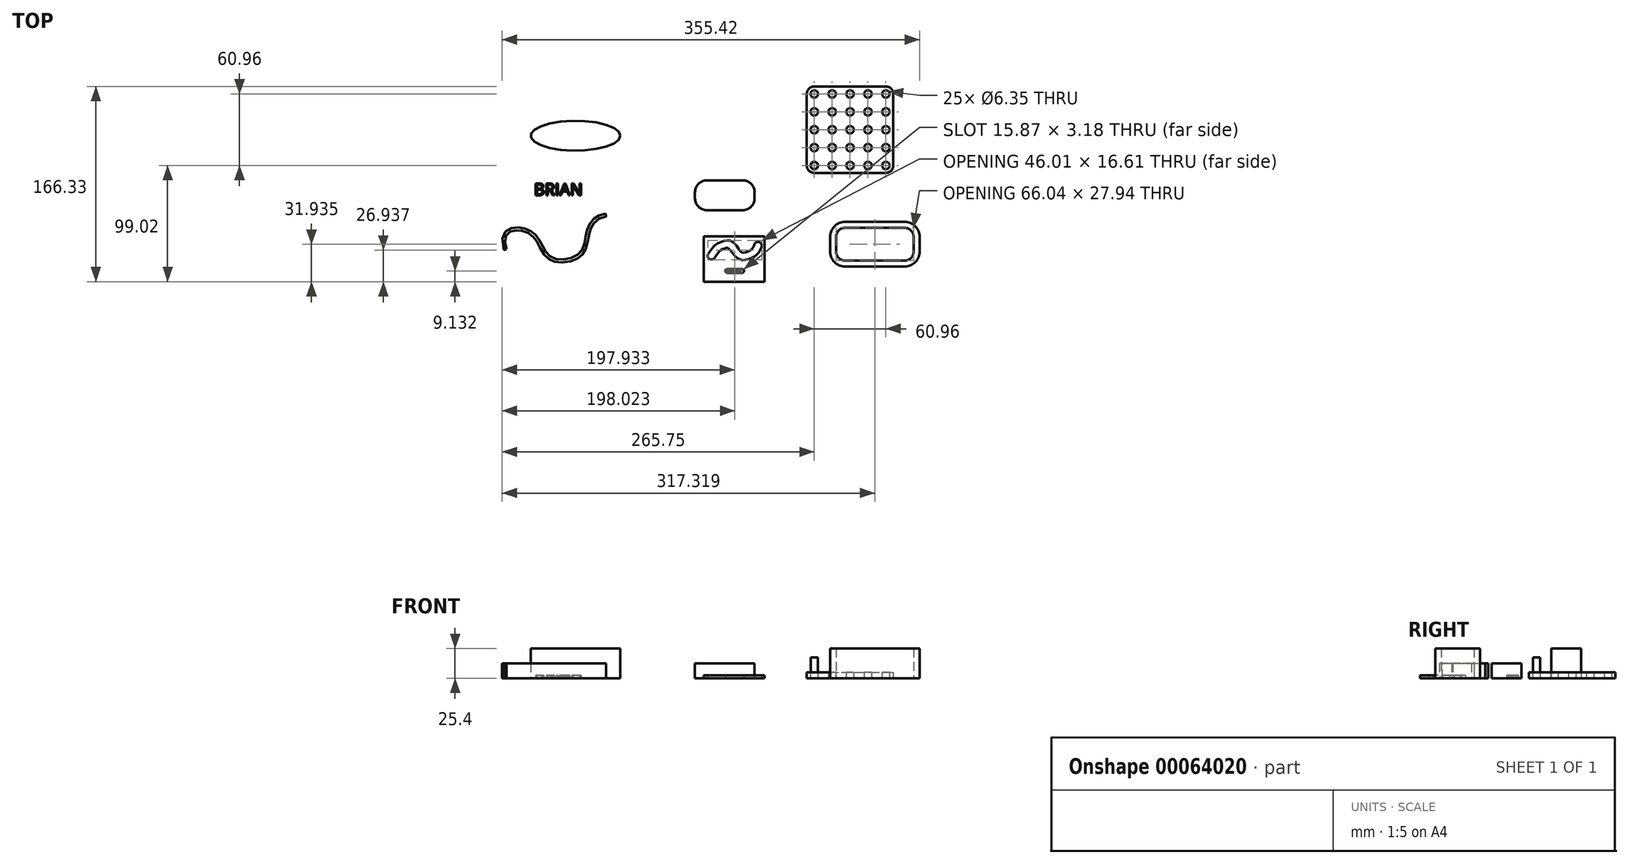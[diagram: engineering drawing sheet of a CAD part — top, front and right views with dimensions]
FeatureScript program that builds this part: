
annotation { "Feature Type Name" : "Feature", "Feature Type Description" : "" }
export const myFeature = defineFeature(function(context is Context, id is Id, definition is map)
    precondition{}
    {
        {
            var Q0;
            Q0=qCreatedBy(makeId("Top.planeOp"),FACE);
            var sketch = newSketch(context, id + "F0", { "sketchPlane" : qUnion([Q0])});
            skLineSegment(sketch, "E0.rect.bottom", {"start": v(15.24, 12.7) * mm, "end": v(-15.24, 12.7) * mm});
            skLineSegment(sketch, "E0.rect.top", {"start": v(15.24, -12.7) * mm, "end": v(-15.24, -12.7) * mm});
            skLineSegment(sketch, "E0.rect.left", {"start": v(25.4, 2.54) * mm, "end": v(25.4, -2.54) * mm});
            skLineSegment(sketch, "E0.rect.right", {"start": v(-25.4, 2.54) * mm, "end": v(-25.4, -2.54) * mm});
            skPoint(sketch, "E0.rect.middle", {"position": v(0, 0) * mm});
            skPoint(sketch, "E1.visualSharp", {"position": v(25.4, 12.7) * mm});
            skArc(sketch, "E1.filletArc", {"start": v(25.4, 2.54) * mm, "mid": v(22.42, 9.72) * mm, "end": v(15.24, 12.7) * mm});
            skPoint(sketch, "E2.visualSharp", {"position": v(25.4, -12.7) * mm});
            skArc(sketch, "E2.filletArc", {"start": v(15.24, -12.7) * mm, "mid": v(22.42, -9.72) * mm, "end": v(25.4, -2.54) * mm});
            skPoint(sketch, "E3.visualSharp", {"position": v(-25.4, 12.7) * mm});
            skArc(sketch, "E3.filletArc", {"start": v(-15.24, 12.7) * mm, "mid": v(-22.42, 9.72) * mm, "end": v(-25.4, 2.54) * mm});
            skPoint(sketch, "E4.visualSharp", {"position": v(-25.4, -12.7) * mm});
            skArc(sketch, "E4.filletArc", {"start": v(-25.4, -2.54) * mm, "mid": v(-22.42, -9.72) * mm, "end": v(-15.24, -12.7) * mm});
            skSolve(sketch);
        }
        {
            var Q0;
            Q0 = qSketchRegion(id + "F0", true);
            extrude(context, id + "F1", {"entities" : qUnion([Q0]), "depth" : 12.7 * mm});
        }
        {
            var Q0;
            Q0=qCreatedBy(makeId("Top.planeOp"),FACE);
            var sketch = newSketch(context, id + "F2", { "sketchPlane" : qUnion([Q0])});
            skCircle(sketch, "E5", {"center": v(76.2, 25.4) * mm, "radius": 3.18 * mm});
            skCircle(sketch, "E6.0.1.0", {"center": v(76.2, 40.64) * mm, "radius": 3.18 * mm});
            skCircle(sketch, "E6.0.2.0", {"center": v(76.2, 55.88) * mm, "radius": 3.18 * mm});
            skCircle(sketch, "E6.0.3.0", {"center": v(76.2, 71.12) * mm, "radius": 3.18 * mm});
            skCircle(sketch, "E6.0.4.0", {"center": v(76.2, 86.36) * mm, "radius": 3.18 * mm});
            skCircle(sketch, "E6.1.0.0", {"center": v(91.44, 25.4) * mm, "radius": 3.18 * mm});
            skCircle(sketch, "E6.1.1.0", {"center": v(91.44, 40.64) * mm, "radius": 3.18 * mm});
            skCircle(sketch, "E6.1.2.0", {"center": v(91.44, 55.88) * mm, "radius": 3.18 * mm});
            skCircle(sketch, "E6.1.3.0", {"center": v(91.44, 71.12) * mm, "radius": 3.18 * mm});
            skCircle(sketch, "E6.1.4.0", {"center": v(91.44, 86.36) * mm, "radius": 3.18 * mm});
            skCircle(sketch, "E6.2.0.0", {"center": v(106.68, 25.4) * mm, "radius": 3.18 * mm});
            skCircle(sketch, "E6.2.1.0", {"center": v(106.68, 40.64) * mm, "radius": 3.18 * mm});
            skCircle(sketch, "E6.2.2.0", {"center": v(106.68, 55.88) * mm, "radius": 3.18 * mm});
            skCircle(sketch, "E6.2.3.0", {"center": v(106.68, 71.12) * mm, "radius": 3.18 * mm});
            skCircle(sketch, "E6.2.4.0", {"center": v(106.68, 86.36) * mm, "radius": 3.18 * mm});
            skCircle(sketch, "E6.3.0.0", {"center": v(121.92, 25.4) * mm, "radius": 3.18 * mm});
            skCircle(sketch, "E6.3.1.0", {"center": v(121.92, 40.64) * mm, "radius": 3.18 * mm});
            skCircle(sketch, "E6.3.2.0", {"center": v(121.92, 55.88) * mm, "radius": 3.18 * mm});
            skCircle(sketch, "E6.3.3.0", {"center": v(121.92, 71.12) * mm, "radius": 3.18 * mm});
            skCircle(sketch, "E6.3.4.0", {"center": v(121.92, 86.36) * mm, "radius": 3.18 * mm});
            skCircle(sketch, "E6.4.0.0", {"center": v(137.16, 25.4) * mm, "radius": 3.18 * mm});
            skCircle(sketch, "E6.4.1.0", {"center": v(137.16, 40.64) * mm, "radius": 3.18 * mm});
            skCircle(sketch, "E6.4.2.0", {"center": v(137.16, 55.88) * mm, "radius": 3.18 * mm});
            skCircle(sketch, "E6.4.3.0", {"center": v(137.16, 71.12) * mm, "radius": 3.18 * mm});
            skCircle(sketch, "E6.4.4.0", {"center": v(137.16, 86.36) * mm, "radius": 3.18 * mm});
            skLineSegment(sketch, "E6.direction1", {"start": v(76.2, 25.4) * mm, "end": v(91.44, 25.4) * mm, "construction": true});
            skLineSegment(sketch, "E6.direction2", {"start": v(76.2, 25.4) * mm, "end": v(76.2, 40.64) * mm, "construction": true});
            skLineSegment(sketch, "E7.bottom", {"start": v(76.2, 92.7) * mm, "end": v(137.16, 92.7) * mm});
            skLineSegment(sketch, "E7.top", {"start": v(76.2, 19.05) * mm, "end": v(137.16, 19.05) * mm});
            skLineSegment(sketch, "E7.left", {"start": v(69.85, 86.36) * mm, "end": v(69.85, 25.4) * mm});
            skLineSegment(sketch, "E7.right", {"start": v(143.5, 86.36) * mm, "end": v(143.5, 25.4) * mm});
            skPoint(sketch, "E8.visualSharp", {"position": v(143.5, 92.7) * mm});
            skArc(sketch, "E8.filletArc", {"start": v(143.5, 86.36) * mm, "mid": v(141.65, 90.85) * mm, "end": v(137.16, 92.7) * mm});
            skPoint(sketch, "E9.visualSharp", {"position": v(143.5, 19.05) * mm});
            skArc(sketch, "E9.filletArc", {"start": v(137.16, 19.05) * mm, "mid": v(141.65, 20.9) * mm, "end": v(143.5, 25.4) * mm});
            skPoint(sketch, "E10.visualSharp", {"position": v(69.85, 19.05) * mm});
            skArc(sketch, "E10.filletArc", {"start": v(69.85, 25.4) * mm, "mid": v(71.7, 20.9) * mm, "end": v(76.2, 19.05) * mm});
            skPoint(sketch, "E11.visualSharp", {"position": v(69.85, 92.7) * mm});
            skArc(sketch, "E11.filletArc", {"start": v(76.2, 92.7) * mm, "mid": v(71.7, 90.85) * mm, "end": v(69.85, 86.36) * mm});
            skSolve(sketch);
        }
        {
            var Q0;
            Q0 = qSketchRegion(id + "F2", true);
            extrude(context, id + "F3", {"entities" : qUnion([Q0]), "depth" : 5.08 * mm});
        }
        {
            var Q0;
            Q0=qCreatedBy(makeId("Top.planeOp"),FACE);
            var sketch = newSketch(context, id + "F4", { "sketchPlane" : qUnion([Q0])});
            skEllipse(sketch, "E12", {"center": v(-127, 50.8) * mm, "majorRadius": 38.1 * mm, "minorRadius": 12.7 * mm, "majorAxis": v(1, 0)});
            skFitSpline(sketch, "E13.0", {"points": [v(-82.63, 49.22) * mm, v(-82.51, 50.8) * mm, v(-82.63, 52.38) * mm, v(-82.97, 53.89) * mm, v(-83.5, 55.3) * mm, v(-84.4, 57) * mm, v(-85.8, 58.84) * mm, v(-87.78, 60.65) * mm, v(-89.99, 62.2) * mm, v(-92.42, 63.55) * mm, v(-94.65, 64.55) * mm, v(-96.55, 65.29) * mm, v(-98.04, 65.8) * mm, v(-99.59, 66.3) * mm, v(-101.7, 66.9) * mm, v(-104.46, 67.59) * mm, v(-107.92, 68.28) * mm, v(-111.53, 68.84) * mm, v(-115.26, 69.29) * mm, v(-119.1, 69.61) * mm, v(-122.36, 69.77) * mm, v(-125, 69.84) * mm, v(-127, 69.86) * mm, v(-129, 69.84) * mm, v(-131.64, 69.77) * mm, v(-134.9, 69.61) * mm, v(-138.74, 69.29) * mm, v(-142.47, 68.84) * mm, v(-146.08, 68.28) * mm, v(-149.54, 67.59) * mm, v(-152.3, 66.9) * mm, v(-154.41, 66.3) * mm, v(-155.96, 65.8) * mm, v(-157.45, 65.29) * mm, v(-159.35, 64.55) * mm, v(-161.58, 63.55) * mm, v(-164.01, 62.2) * mm, v(-166.22, 60.65) * mm, v(-168.2, 58.84) * mm, v(-169.6, 57) * mm, v(-170.5, 55.3) * mm, v(-171.03, 53.89) * mm, v(-171.37, 52.38) * mm, v(-171.49, 50.8) * mm, v(-171.37, 49.22) * mm, v(-171.03, 47.71) * mm, v(-170.5, 46.3) * mm, v(-169.6, 44.6) * mm, v(-168.2, 42.76) * mm, v(-166.22, 40.95) * mm, v(-164.01, 39.4) * mm, v(-161.58, 38.05) * mm, v(-159.35, 37.05) * mm, v(-157.45, 36.31) * mm, v(-155.96, 35.8) * mm, v(-154.41, 35.3) * mm, v(-152.3, 34.7) * mm, v(-149.54, 34.01) * mm, v(-146.08, 33.32) * mm, v(-142.47, 32.76) * mm, v(-138.74, 32.31) * mm, v(-134.9, 31.99) * mm, v(-131.64, 31.83) * mm, v(-129, 31.76) * mm, v(-127, 31.74) * mm, v(-125, 31.76) * mm, v(-122.36, 31.83) * mm, v(-119.1, 31.99) * mm, v(-115.26, 32.31) * mm, v(-111.53, 32.76) * mm, v(-107.92, 33.32) * mm, v(-104.46, 34.01) * mm, v(-101.7, 34.7) * mm, v(-99.59, 35.3) * mm, v(-98.04, 35.8) * mm, v(-96.55, 36.31) * mm, v(-94.65, 37.05) * mm, v(-92.42, 38.05) * mm, v(-89.99, 39.4) * mm, v(-87.78, 40.95) * mm, v(-85.8, 42.76) * mm, v(-84.4, 44.6) * mm, v(-83.5, 46.3) * mm, v(-82.97, 47.71) * mm, v(-82.63, 49.22) * mm, v(-82.51, 50.8) * mm, v(-82.63, 52.38) * mm, v(-82.63, 49.22) * mm]});
            skSolve(sketch);
        }
        {
            var Q0;
            Q0 = qSketchRegion(id + "F4", true);
            extrude(context, id + "F5", {"entities" : qUnion([Q0]), "depth" : 25.4 * mm});
        }
        {
            var Q0;
            Q0=qCreatedBy(makeId("Top.planeOp"),FACE);
            var sketch = newSketch(context, id + "F6", { "sketchPlane" : qUnion([Q0])});
            skText(sketch, "E14", { "text": "BRIAN", "fontName": "OpenSans-Regular.ttf"});
            const initialGuessF6  = {"E14": [-0.16248, 0, 1, 0, 0.01016]};
            skSetInitialGuess(sketch, initialGuessF6);
            skSolve(sketch);
        }
        {
            var Q0;
            Q0 = qSketchRegion(id + "F6", true);
            extrude(context, id + "F7", {"entities" : qUnion([Q0]), "depth" : 2.54 * mm});
        }
        {
            var Q0;
            Q0=qCreatedBy(makeId("Top.planeOp"),FACE);
            var sketch = newSketch(context, id + "F8", { "sketchPlane" : qUnion([Q0])});
            skFitSpline(sketch, "E15", {"points": [v(-188.2, -46.66) * mm, v(-176, -27.4) * mm, v(-159.05, -36.2) * mm, v(-147.36, -52.89) * mm, v(-123.46, -48.9) * mm, v(-116.84, -27.9) * mm, v(-101.3, -15.54) * mm], "startDerivative": vector(-84.93, 280.28) * mm, "endDerivative": vector(141.44, 19.5) * mm});
            skFitSpline(sketch, "E16.0", {"points": [v(-185.76, -45.92) * mm, v(-186.18, -44.55) * mm, v(-186.78, -42.04) * mm, v(-187.09, -38.94) * mm, v(-186.9, -36.49) * mm, v(-186.36, -34.62) * mm, v(-185.55, -33.2) * mm, v(-184.51, -32.11) * mm, v(-183.22, -31.25) * mm, v(-181.67, -30.6) * mm, v(-179.92, -30.16) * mm, v(-178.03, -29.94) * mm, v(-176.42, -29.91) * mm, v(-175.15, -29.97) * mm, v(-173.92, -30.08) * mm, v(-172.42, -30.32) * mm, v(-170.13, -30.9) * mm, v(-167.48, -31.97) * mm, v(-165.14, -33.48) * mm, v(-163.45, -34.94) * mm, v(-162.47, -35.96) * mm, v(-161.74, -36.83) * mm, v(-161.22, -37.52) * mm, v(-160.73, -38.23) * mm, v(-160.08, -39.25) * mm, v(-159.31, -40.6) * mm, v(-158.12, -42.93) * mm, v(-156.6, -46.03) * mm, v(-154.84, -49.13) * mm, v(-153.07, -51.47) * mm, v(-151.52, -53.1) * mm, v(-150, -54.3) * mm, v(-148.62, -55.11) * mm, v(-147.16, -55.82) * mm, v(-145.22, -56.5) * mm, v(-142.77, -57.01) * mm, v(-140.23, -57.25) * mm, v(-136.76, -57.23) * mm, v(-133.27, -56.72) * mm, v(-129.91, -55.75) * mm, v(-127.5, -54.8) * mm, v(-125.24, -53.6) * mm, v(-123.52, -52.41) * mm, v(-122.27, -51.33) * mm, v(-121.4, -50.44) * mm, v(-120.62, -49.5) * mm, v(-119.7, -48.2) * mm, v(-118.77, -46.5) * mm, v(-117.64, -43.68) * mm, v(-116.77, -40.06) * mm, v(-116.2, -36.5) * mm, v(-115.74, -33.78) * mm, v(-115.35, -31.82) * mm, v(-114.96, -30.29) * mm, v(-114.59, -29.13) * mm, v(-114.18, -28.03) * mm, v(-113.57, -26.7) * mm, v(-112.69, -25.22) * mm, v(-111.67, -23.84) * mm, v(-110.13, -22.17) * mm, v(-107.89, -20.4) * mm, v(-104.7, -18.84) * mm, v(-102.25, -18.23) * mm, v(-100.95, -18.05) * mm]});
            skLineSegment(sketch, "E17", {"start": v(-188.2, -46.66) * mm, "end": v(-185.76, -45.92) * mm});
            skLineSegment(sketch, "E18", {"start": v(-100.95, -18.05) * mm, "end": v(-101.3, -15.54) * mm});
            skSolve(sketch);
        }
        {
            var Q0;
            Q0 = qSketchRegion(id + "F8", true);
            extrude(context, id + "F9", {"entities" : qUnion([Q0]), "depth" : 12.7 * mm});
        }
        {
            var Q0;
            Q0=qCreatedBy(makeId("Top.planeOp"),FACE);
            var sketch = newSketch(context, id + "F10", { "sketchPlane" : qUnion([Q0])});
            skLineSegment(sketch, "E19.bottom", {"start": v(102.37, -22.64) * mm, "end": v(153.17, -22.64) * mm});
            skLineSegment(sketch, "E19.top", {"start": v(102.37, -60.74) * mm, "end": v(153.17, -60.74) * mm});
            skLineSegment(sketch, "E19.left", {"start": v(89.67, -35.34) * mm, "end": v(89.67, -48.04) * mm});
            skLineSegment(sketch, "E19.right", {"start": v(165.87, -35.34) * mm, "end": v(165.87, -48.04) * mm});
            skPoint(sketch, "E20.visualSharp", {"position": v(89.67, -22.64) * mm});
            skArc(sketch, "E20.filletArc", {"start": v(102.37, -22.64) * mm, "mid": v(93.39, -26.36) * mm, "end": v(89.67, -35.34) * mm});
            skPoint(sketch, "E21.visualSharp", {"position": v(165.87, -22.64) * mm});
            skArc(sketch, "E21.filletArc", {"start": v(165.87, -35.34) * mm, "mid": v(162.15, -26.36) * mm, "end": v(153.17, -22.64) * mm});
            skPoint(sketch, "E22.visualSharp", {"position": v(165.87, -60.74) * mm});
            skArc(sketch, "E22.filletArc", {"start": v(153.17, -60.74) * mm, "mid": v(162.15, -57.02) * mm, "end": v(165.87, -48.04) * mm});
            skPoint(sketch, "E23.visualSharp", {"position": v(89.67, -60.74) * mm});
            skArc(sketch, "E23.filletArc", {"start": v(89.67, -48.04) * mm, "mid": v(93.39, -57.02) * mm, "end": v(102.37, -60.74) * mm});
            skArc(sketch, "E24.0", {"start": v(102.37, -27.72) * mm, "mid": v(96.98, -29.95) * mm, "end": v(94.75, -35.34) * mm});
            skLineSegment(sketch, "E24.1", {"start": v(94.75, -35.34) * mm, "end": v(94.75, -48.04) * mm});
            skLineSegment(sketch, "E24.2", {"start": v(102.37, -27.72) * mm, "end": v(153.17, -27.72) * mm});
            skArc(sketch, "E24.3", {"start": v(94.75, -48.04) * mm, "mid": v(96.98, -53.42) * mm, "end": v(102.37, -55.66) * mm});
            skArc(sketch, "E24.4", {"start": v(160.79, -35.34) * mm, "mid": v(158.56, -29.95) * mm, "end": v(153.17, -27.72) * mm});
            skLineSegment(sketch, "E24.5", {"start": v(160.79, -35.34) * mm, "end": v(160.79, -48.04) * mm});
            skArc(sketch, "E24.6", {"start": v(153.17, -55.66) * mm, "mid": v(158.56, -53.42) * mm, "end": v(160.79, -48.04) * mm});
            skLineSegment(sketch, "E24.7", {"start": v(102.37, -55.66) * mm, "end": v(153.17, -55.66) * mm});
            skSolve(sketch);
        }
        {
            var Q0;
            Q0 = qSketchRegion(id + "F10", true);
            extrude(context, id + "F11", {"entities" : qUnion([Q0]), "depth" : 25.4 * mm});
        }
        {
            var Q0;
            Q0=qCreatedBy(makeId("Top.planeOp"),FACE);
            var sketch = newSketch(context, id + "F12", { "sketchPlane" : qUnion([Q0])});
            skFitSpline(sketch, "E25", {"points": [v(-11.4, -51.6) * mm, v(-6.26, -44.96) * mm, v(-1.64, -42.42) * mm, v(3.92, -41.86) * mm, v(9.67, -48.14) * mm, v(14.97, -51.92) * mm, v(20.5, -51.01) * mm, v(24.98, -48.32) * mm, v(28.3, -42.84) * mm], "startDerivative": vector(23.75, 39.1) * mm, "endDerivative": vector(12.63, 30.6) * mm, "construction": true});
            skArc(sketch, "E26.0.startCap", {"start": v(-8.68, -53.24) * mm, "mid": v(-13.04, -54.3) * mm, "end": v(-14.1, -49.95) * mm});
            skArc(sketch, "E26.0.endCap", {"start": v(25.37, -41.62) * mm, "mid": v(29.51, -39.9) * mm, "end": v(31.24, -44.05) * mm});
            skFitSpline(sketch, "E26.0.left", {"points": [v(-14.1, -49.95) * mm, v(-13.84, -49.5) * mm, v(-13.24, -48.55) * mm, v(-12.18, -47) * mm, v(-11.19, -45.67) * mm, v(-10.34, -44.63) * mm, v(-9.68, -43.88) * mm, v(-9.11, -43.28) * mm, v(-8.64, -42.82) * mm, v(-8.15, -42.38) * mm, v(-7.53, -41.87) * mm, v(-6.54, -41.16) * mm, v(-5.54, -40.6) * mm, v(-4.56, -40.15) * mm, v(-3.85, -39.85) * mm, v(-3.28, -39.64) * mm, v(-2.82, -39.47) * mm, v(-2.37, -39.3) * mm, v(-1.75, -39.09) * mm, v(-0.66, -38.75) * mm, v(0.58, -38.46) * mm, v(1.98, -38.34) * mm, v(2.92, -38.37) * mm, v(3.7, -38.5) * mm, v(4.3, -38.63) * mm, v(4.9, -38.82) * mm, v(5.7, -39.16) * mm, v(6.57, -39.68) * mm, v(7.48, -40.38) * mm, v(8.28, -41.14) * mm, v(9.24, -42.2) * mm, v(10.3, -43.56) * mm, v(11.24, -44.89) * mm, v(11.92, -45.85) * mm, v(12.56, -46.71) * mm, v(13.28, -47.58) * mm, v(13.88, -48.14) * mm, v(14.29, -48.42) * mm, v(14.58, -48.57) * mm, v(14.87, -48.68) * mm, v(15.15, -48.75) * mm, v(15.42, -48.78) * mm, v(15.74, -48.8) * mm, v(16.22, -48.8) * mm, v(16.9, -48.72) * mm, v(17.88, -48.54) * mm, v(19.2, -48.14) * mm, v(20.5, -47.56) * mm, v(21.46, -47.02) * mm, v(22.1, -46.6) * mm, v(22.65, -46.16) * mm, v(23.1, -45.74) * mm, v(23.5, -45.28) * mm, v(23.97, -44.63) * mm, v(24.46, -43.77) * mm, v(24.94, -42.7) * mm, v(25.22, -41.99) * mm, v(25.37, -41.62) * mm]});
            skFitSpline(sketch, "E26.0.right", {"points": [v(-8.68, -53.24) * mm, v(-8.45, -52.87) * mm, v(-7.93, -52.04) * mm, v(-7, -50.68) * mm, v(-6.17, -49.56) * mm, v(-5.5, -48.73) * mm, v(-4.99, -48.16) * mm, v(-4.59, -47.74) * mm, v(-4.29, -47.45) * mm, v(-4, -47.2) * mm, v(-3.67, -46.92) * mm, v(-3.15, -46.55) * mm, v(-2.62, -46.25) * mm, v(-2.02, -45.97) * mm, v(-1.52, -45.76) * mm, v(-1.06, -45.59) * mm, v(-0.66, -45.44) * mm, v(-0.24, -45.29) * mm, v(0.26, -45.12) * mm, v(0.82, -44.94) * mm, v(1.33, -44.81) * mm, v(1.78, -44.73) * mm, v(2.15, -44.7) * mm, v(2.38, -44.71) * mm, v(2.52, -44.74) * mm, v(2.6, -44.76) * mm, v(2.68, -44.78) * mm, v(2.77, -44.82) * mm, v(2.97, -44.93) * mm, v(3.31, -45.2) * mm, v(3.73, -45.58) * mm, v(4.34, -46.24) * mm, v(5.17, -47.3) * mm, v(6.22, -48.79) * mm, v(7.32, -50.34) * mm, v(8.54, -51.84) * mm, v(9.78, -53.02) * mm, v(10.97, -53.85) * mm, v(11.97, -54.38) * mm, v(13.06, -54.8) * mm, v(14.04, -55.01) * mm, v(14.84, -55.1) * mm, v(15.65, -55.16) * mm, v(16.65, -55.14) * mm, v(17.85, -55) * mm, v(19.45, -54.7) * mm, v(21.42, -54.1) * mm, v(23.33, -53.26) * mm, v(24.78, -52.44) * mm, v(25.82, -51.75) * mm, v(26.63, -51.11) * mm, v(27.25, -50.55) * mm, v(27.83, -49.97) * mm, v(28.47, -49.24) * mm, v(29.33, -48.05) * mm, v(30.15, -46.6) * mm, v(30.82, -45.09) * mm, v(31.12, -44.32) * mm, v(31.24, -44.05) * mm]});
            skLineSegment(sketch, "E27", {"start": v(2.03, -64.49) * mm, "end": v(14.73, -64.49) * mm, "construction": true});
            skArc(sketch, "E28.0.startCap", {"start": v(2.03, -66.08) * mm, "mid": v(0.45, -64.49) * mm, "end": v(2.03, -62.9) * mm});
            skArc(sketch, "E28.0.endCap", {"start": v(14.73, -62.9) * mm, "mid": v(16.32, -64.49) * mm, "end": v(14.73, -66.08) * mm});
            skLineSegment(sketch, "E28.0.left", {"start": v(2.03, -62.9) * mm, "end": v(14.73, -62.9) * mm});
            skLineSegment(sketch, "E28.0.right", {"start": v(2.03, -66.08) * mm, "end": v(14.73, -66.08) * mm});
            skLineSegment(sketch, "E29.bottom", {"start": v(-17.78, -34.99) * mm, "end": v(33.96, -34.99) * mm});
            skLineSegment(sketch, "E29.top", {"start": v(-17.78, -73.62) * mm, "end": v(33.96, -73.62) * mm});
            skLineSegment(sketch, "E29.left", {"start": v(-17.78, -34.99) * mm, "end": v(-17.78, -73.62) * mm});
            skLineSegment(sketch, "E29.right", {"start": v(33.96, -34.99) * mm, "end": v(33.96, -73.62) * mm});
            skSolve(sketch);
        }
        {
            var Q0;
            Q0 = qSketchRegion(id + "F12", true);
            extrude(context, id + "F13", {"entities" : qUnion([Q0]), "depth" : 2.54 * mm});
        }
        {
            var Q0;
            Q0=makeQuery(id+"F3.opExtrude","CAP_FACE",FACE,{"disambiguationData":[OSD([sQuery(id+"F2.wireOp",EDGE,"E5"),sQuery(id+"F2.wireOp",EDGE,"E6.0.1.0"),sQuery(id+"F2.wireOp",EDGE,"E6.0.2.0"),sQuery(id+"F2.wireOp",EDGE,"E6.0.3.0"),sQuery(id+"F2.wireOp",EDGE,"E6.0.4.0"),sQuery(id+"F2.wireOp",EDGE,"E6.1.0.0"),sQuery(id+"F2.wireOp",EDGE,"E6.1.1.0"),sQuery(id+"F2.wireOp",EDGE,"E6.1.2.0"),sQuery(id+"F2.wireOp",EDGE,"E6.1.3.0"),sQuery(id+"F2.wireOp",EDGE,"E6.1.4.0"),sQuery(id+"F2.wireOp",EDGE,"E6.2.0.0"),sQuery(id+"F2.wireOp",EDGE,"E6.2.1.0"),sQuery(id+"F2.wireOp",EDGE,"E6.2.2.0"),sQuery(id+"F2.wireOp",EDGE,"E6.2.3.0"),sQuery(id+"F2.wireOp",EDGE,"E6.2.4.0"),sQuery(id+"F2.wireOp",EDGE,"E6.3.0.0"),sQuery(id+"F2.wireOp",EDGE,"E6.3.1.0"),sQuery(id+"F2.wireOp",EDGE,"E6.3.2.0"),sQuery(id+"F2.wireOp",EDGE,"E6.3.3.0"),sQuery(id+"F2.wireOp",EDGE,"E6.3.4.0"),sQuery(id+"F2.wireOp",EDGE,"E6.4.0.0"),sQuery(id+"F2.wireOp",EDGE,"E6.4.1.0"),sQuery(id+"F2.wireOp",EDGE,"E6.4.2.0"),sQuery(id+"F2.wireOp",EDGE,"E6.4.3.0"),sQuery(id+"F2.wireOp",EDGE,"E6.4.4.0"),sQuery(id+"F2.wireOp",EDGE,"E7.bottom"),sQuery(id+"F2.wireOp",EDGE,"E7.top"),sQuery(id+"F2.wireOp",EDGE,"E7.left"),sQuery(id+"F2.wireOp",EDGE,"E7.right"),sQuery(id+"F2.wireOp",EDGE,"E8.filletArc"),sQuery(id+"F2.wireOp",EDGE,"E9.filletArc"),sQuery(id+"F2.wireOp",EDGE,"E10.filletArc"),sQuery(id+"F2.wireOp",EDGE,"E11.filletArc")])],"isStart":false});
            var sketch = newSketch(context, id + "F14", { "sketchPlane" : qUnion([Q0])});
            skCircle(sketch, "E30", {"center": v(76.2, 25.4) * mm, "radius": 3.05 * mm});
            skSolve(sketch);
        }
        {
            var Q0;
            Q0 = qSketchRegion(id + "F14", true);
            extrude(context, id + "F15", {"entities" : qUnion([Q0]), "depth" : 12.7 * mm});
        }
    });
